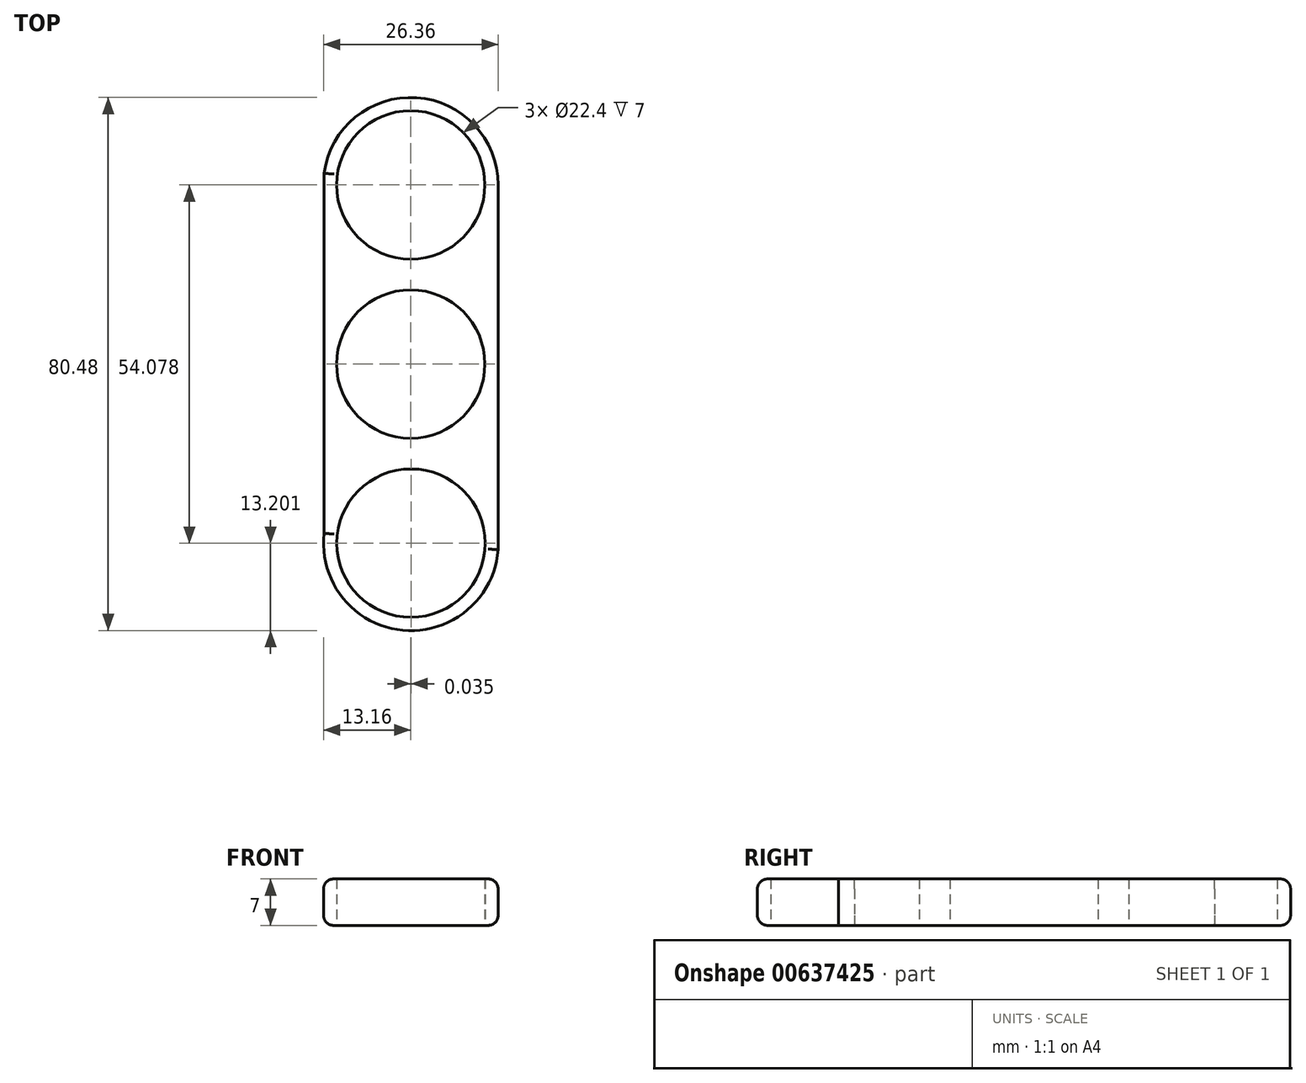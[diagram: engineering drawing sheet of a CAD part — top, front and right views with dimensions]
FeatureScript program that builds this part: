
annotation { "Feature Type Name" : "Feature", "Feature Type Description" : "" }
export const myFeature = defineFeature(function(context is Context, id is Id, definition is map)
    precondition{}
    {
        {
            var Q0;
            Q0=qCreatedBy(makeId("Top.planeOp"),FACE);
            var sketch = newSketch(context, id + "F0", { "sketchPlane" : qUnion([Q0])});
            skCircle(sketch, "E0", {"center": v(0, 0) * mm, "radius": 11.2 * mm});
            skArc(sketch, "E1", {"start": v(-13.08, 1.75) * mm, "mid": v(-13.2, 0) * mm, "end": v(-13.08, -1.75) * mm});
            skCircle(sketch, "E2", {"center": v(0, 27.04) * mm, "radius": 11.2 * mm});
            skArc(sketch, "E3", {"start": v(13.2, 27.04) * mm, "mid": v(-0.88, 40.2) * mm, "end": v(-13.08, 25.29) * mm});
            skArc(sketch, "E4.1.0", {"start": v(-13.08, -25.57) * mm, "mid": v(-0.22, -40.24) * mm, "end": v(13.2, -26.08) * mm});
            skCircle(sketch, "E4.1.1", {"center": v(0.04, -27.04) * mm, "radius": 11.2 * mm});
            skPoint(sketch, "E4.center", {"position": v(0.02, 0) * mm});
            skLineSegment(sketch, "E5", {"start": v(-13.08, 28.8) * mm, "end": v(-13.08, -27.04) * mm});
            skLineSegment(sketch, "E6", {"start": v(13.2, 27.04) * mm, "end": v(13.2, -28) * mm});
            skSolve(sketch);
        }
        {
            var Q0;
            Q0=makeQuery(id+"F0.imprint","IMPRINT",FACE,{"disambiguationData":[TD([[makeQuery(id+"F0.imprint","IMPRINT",EDGE,{"derivedFrom":sQuery(id+"F0.wireOp",EDGE,"E0")}),-1.0]])]});
            extrude(context, id + "F1", {"entities" : qUnion([Q0]), "depth" : 7 * mm, "offsetDistance" : 25 * mm});
        }
        {
            var Q0;
            Q0=makeQuery(id+"F1.opExtrude","CAP_EDGE",EDGE,{"disambiguationData":[OSD([sQuery(id+"F0.wireOp",EDGE,"E4.1.0")])],"isStart":false});
            var Q1;
            Q1=makeQuery(id+"F1.opExtrude","CAP_EDGE",EDGE,{"disambiguationData":[OSD([sQuery(id+"F0.wireOp",EDGE,"E5")])],"isStart":false});
            var Q2;
            Q2=makeQuery(id+"F1.opExtrude","CAP_EDGE",EDGE,{"disambiguationData":[OSD([sQuery(id+"F0.wireOp",EDGE,"E6")])],"isStart":false});
            var Q3;
            Q3=makeQuery(id+"F1.opExtrude","CAP_EDGE",EDGE,{"disambiguationData":[OSD([sQuery(id+"F0.wireOp",EDGE,"E3")])],"isStart":false});
            fillet(context, id + "F2", {"entities" : qUnion([Q0, Q1, Q2, Q3]), "radius" : 1.5 * mm, "tangentPropagation" : true, "allowEdgeOverflow" : false});
        }
        {
            var Q0;
            Q0=makeQuery(id+"F1.opExtrude","CAP_EDGE",EDGE,{"disambiguationData":[OSD([sQuery(id+"F0.wireOp",EDGE,"E4.1.0")])],"isStart":true});
            var Q1;
            Q1=makeQuery(id+"F1.opExtrude","CAP_EDGE",EDGE,{"disambiguationData":[OSD([sQuery(id+"F0.wireOp",EDGE,"E5")])],"isStart":true});
            var Q2;
            Q2=makeQuery(id+"F1.opExtrude","CAP_EDGE",EDGE,{"disambiguationData":[OSD([sQuery(id+"F0.wireOp",EDGE,"E6")])],"isStart":true});
            var Q3;
            Q3=makeQuery(id+"F1.opExtrude","CAP_EDGE",EDGE,{"disambiguationData":[OSD([sQuery(id+"F0.wireOp",EDGE,"E3")])],"isStart":true});
            fillet(context, id + "F3", {"entities" : qUnion([Q0, Q1, Q2, Q3]), "radius" : 1.5 * mm, "tangentPropagation" : true, "allowEdgeOverflow" : false});
        }
    });
